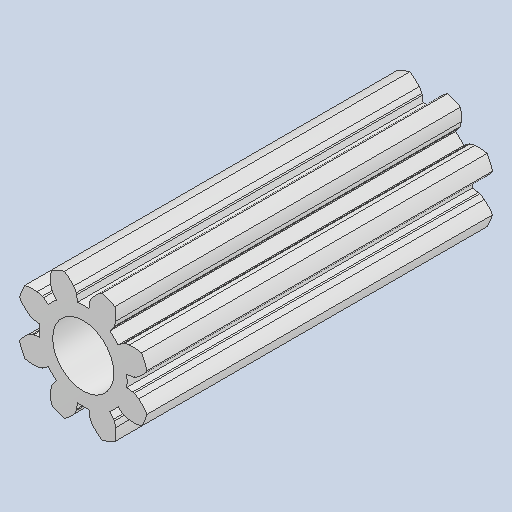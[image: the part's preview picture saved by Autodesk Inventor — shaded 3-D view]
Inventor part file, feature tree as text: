
AUTODESK INVENTOR PART (.ipt)
format: ipt  version: 2023 (Build 270158030, 158C)  size: 275,968 bytes
history: native  units: mm
features: other x3, sketch x1
ambient origin geometry x8: Origin, YZ Plane, XZ Plane, XY Plane, X Axis, Y Axis, Z Axis, Center Point
bodies: Solid2 (feature_tree)
feature tree (4):
  other  "ぴにょん.ipt"
  other  "Solid2::ぴにょん.ipt"
  other  "TaggingFeature1"
  sketch  "Sketch2"  dims[d0=10.0mm]
